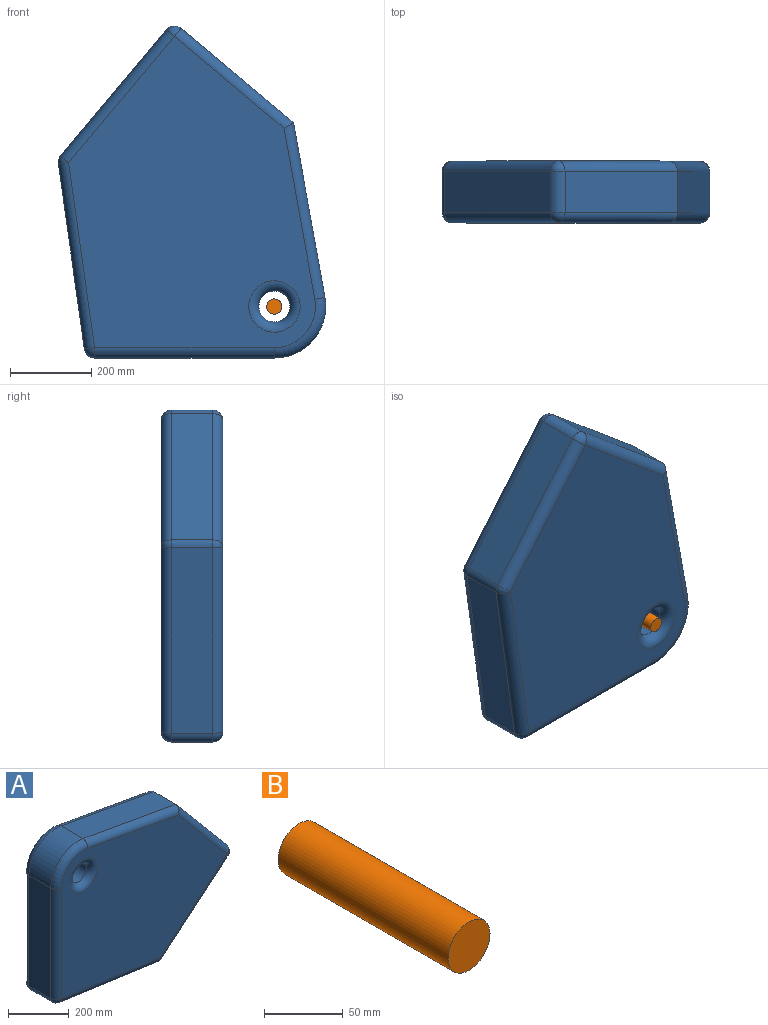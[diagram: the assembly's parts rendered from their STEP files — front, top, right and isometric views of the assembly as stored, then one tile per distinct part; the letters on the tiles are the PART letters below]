
ASSEMBLY  parts=2 mates=1
PART A: 32 faces, bbox 829.8x152.4x670.7 mm
  f0: plane 311.32x261.23mm, normal (0.64,0,-0.77), area 41290.2mm2, adj f7,f11,f18,f29
  f1: plane 277.56x232.9mm, normal (0.77,0,0.64), area 36812mm2, adj f2,f11,f22,f30
  f2: plane 430.94x101.6mm, normal (0.18,0,0.98), area 44489.9mm2, adj f1,f3,f21,f28
  f3: cylinder r=127mm len=149.54mm, axis (0,1,0), area 22570.7mm2, adj f2,f4,f19,f26
  f4: plane 443.59x101.6mm, normal (-1,0,0), area 45069.2mm2, adj f3,f5,f17,f24
  f5: cylinder r=25.4mm len=101.6mm, axis (0,1,0), area 3693.3mm2, adj f4,f6,f15,f23
  f6: plane 457.2x101.6mm, normal (-0.14,0,-0.99), area 46908mm2, adj f5,f7,f14,f25
  f7: cylinder r=25.4mm len=101.6mm, axis (0,1,0), area 2162mm2, adj f0,f6,f16,f27
  f8: plane 768.52x609.45mm, normal (0,1,0), area 333057.9mm2, adj f13,f14,f17,f18,f19,f21,f22
  f9: plane 768.52x609.45mm, normal (0,-1,0), area 333057.9mm2, adj f12,f24,f25,f26,f28,f29,f30
  f10: cylinder r=38.1mm len=101.6mm, axis (0,-1,0), area 24322mm2, adj f12,f13
  f11: cylinder r=25.4mm len=101.6mm, axis (0,1,0), area 4053.7mm2, adj f0,f1,f20,f31
  f12: torus R=63.5mm, axis (0,-1,0), area 11865mm2, adj f9,f10
  f13: torus R=63.5mm, axis (0,-1,0), area 11865mm2, adj f8,f10
  f14: cylinder r=25.4mm len=460.74mm, axis (0.99,0,-0.14), area 18420.7mm2, adj f6,f8,f15,f16
  f15: sphere r=25.4mm, area 923.3mm2, adj f5,f14,f17
  f16: sphere r=25.4mm, area 540.5mm2, adj f7,f14,f18
  f17: cylinder r=25.4mm len=443.59mm, axis (0,0,-1), area 17698.6mm2, adj f4,f8,f15,f19
  f18: cylinder r=25.4mm len=327.65mm, axis (0.77,0,0.64), area 16214.6mm2, adj f0,f8,f16,f20
  f19: torus R=101.6mm, axis (0,-1,0), area 8219.3mm2, adj f3,f8,f17,f21
  f20: sphere r=25.4mm, area 1013.4mm2, adj f11,f18,f22
  f21: cylinder r=25.4mm len=435.45mm, axis (-0.98,0,0.18), area 17337.9mm2, adj f2,f8,f19,f22
  f22: cylinder r=25.4mm len=293.88mm, axis (-0.64,0,0.77), area 14322.8mm2, adj f1,f8,f20,f21
  f23: sphere r=25.4mm, area 923.3mm2, adj f5,f24,f25
  f24: cylinder r=25.4mm len=443.59mm, axis (0,0,1), area 17698.6mm2, adj f4,f9,f23,f26
  f25: cylinder r=25.4mm len=460.74mm, axis (-0.99,0,0.14), area 18420.7mm2, adj f6,f9,f23,f27
  f26: torus R=101.6mm, axis (0,-1,0), area 8219.3mm2, adj f3,f9,f24,f28
  f27: sphere r=25.4mm, area 540.5mm2, adj f7,f25,f29
  f28: cylinder r=25.4mm len=435.45mm, axis (0.98,0,-0.18), area 17337.9mm2, adj f2,f9,f26,f30
  f29: cylinder r=25.4mm len=327.65mm, axis (-0.77,0,-0.64), area 16214.6mm2, adj f0,f9,f27,f31
  f30: cylinder r=25.4mm len=293.88mm, axis (0.64,0,-0.77), area 14322.8mm2, adj f1,f9,f28,f31
  f31: sphere r=25.4mm, area 1013.4mm2, adj f11,f29,f30
PART B: 3 faces, bbox 37.6x152.4x37.6 mm
  f0: cylinder r=18.81mm len=152.4mm, axis (0,1,0), area 18007.6mm2, adj f1,f2
  f1: plane 37.61x37.61mm, normal (0,-1,0), area 1111mm2, adj f0
  f2: plane 37.61x37.61mm, normal (0,1,0), area 1111mm2, adj f0
PLACE A rot(axis=(0.71,0,0.71),180deg) t=(-507.85,-12.7,355.6)mm
PLACE B at identity fixed
MATE revolute B.f0 <-> A.f3  axis (0,1,0) through (0,0,0)mm
